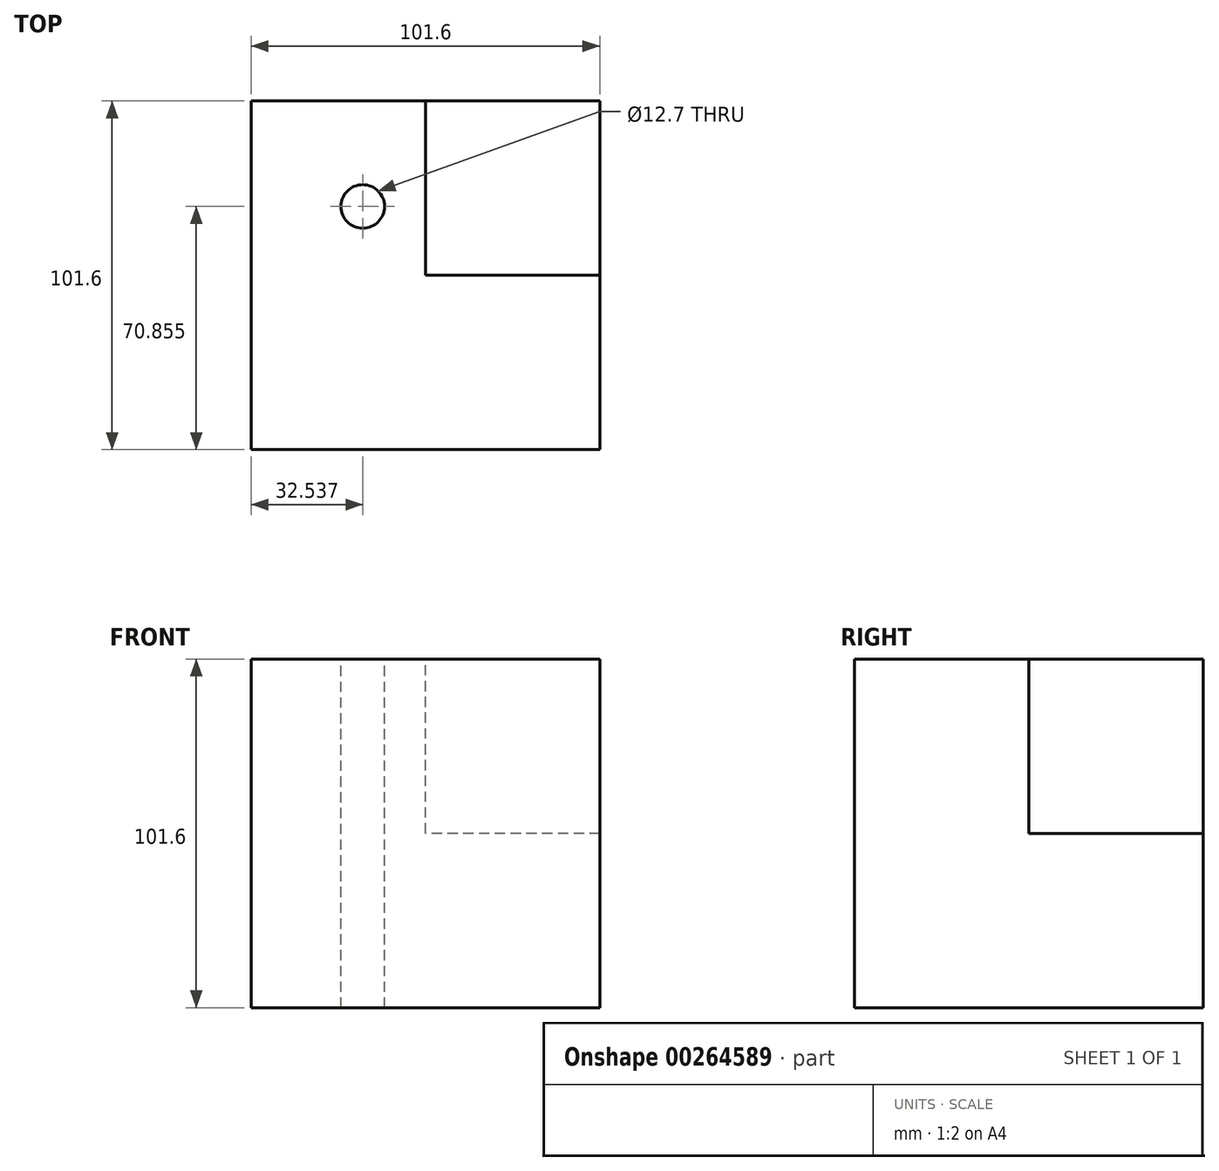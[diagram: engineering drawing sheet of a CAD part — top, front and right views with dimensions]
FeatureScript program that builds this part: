
annotation { "Feature Type Name" : "Feature", "Feature Type Description" : "" }
export const myFeature = defineFeature(function(context is Context, id is Id, definition is map)
    precondition{}
    {
        {
            var Q0;
            Q0=qCreatedBy(makeId("Front.planeOp"),FACE);
            var sketch = newSketch(context, id + "F0", { "sketchPlane" : qUnion([Q0])});
            skLineSegment(sketch, "E0.bottom", {"start": v(0, 0) * mm, "end": v(-101.6, 0) * mm});
            skLineSegment(sketch, "E0.top", {"start": v(0, 101.6) * mm, "end": v(-101.6, 101.6) * mm});
            skLineSegment(sketch, "E0.left", {"start": v(0, 0) * mm, "end": v(0, 101.6) * mm});
            skLineSegment(sketch, "E0.right", {"start": v(-101.6, 0) * mm, "end": v(-101.6, 101.6) * mm});
            skSolve(sketch);
        }
        {
            var Q0;
            Q0 = qSketchRegion(id + "F0", true);
            extrude(context, id + "F1", {"entities" : qUnion([Q0]), "depth" : 101.6 * mm});
        }
        {
            var Q0;
            Q0=makeQuery(id+"F1.opExtrude","SWEPT_FACE",FACE,{"disambiguationData":[OSD([sQuery(id+"F0.wireOp",EDGE,"E0.top")])]});
            var sketch = newSketch(context, id + "F2", { "sketchPlane" : qUnion([Q0])});
            skCircle(sketch, "E1", {"center": v(-69.06, -30.75) * mm, "radius": 6.35 * mm});
            skSolve(sketch);
        }
        {
            var Q0;
            Q0 = qSketchRegion(id + "F2", true);
            extrude(context, id + "F3", {"entities" : qUnion([Q0]), "operationType" : NewBodyOperationType.REMOVE, "oppositeDirection" : true, "depth" : 101.6 * mm});
        }
        {
            var Q0;
            Q0=makeQuery(id+"F1.opExtrude","SWEPT_FACE",FACE,{"disambiguationData":[OSD([sQuery(id+"F0.wireOp",EDGE,"E0.top")])]});
            var sketch = newSketch(context, id + "F4", { "sketchPlane" : qUnion([Q0])});
            skLineSegment(sketch, "E2.bottom", {"start": v(0, 0) * mm, "end": v(-50.8, 0) * mm});
            skLineSegment(sketch, "E2.top", {"start": v(0, -50.8) * mm, "end": v(-50.8, -50.8) * mm});
            skLineSegment(sketch, "E2.left", {"start": v(0, 0) * mm, "end": v(0, -50.8) * mm});
            skLineSegment(sketch, "E2.right", {"start": v(-50.8, 0) * mm, "end": v(-50.8, -50.8) * mm});
            skSolve(sketch);
        }
        {
            var Q0;
            Q0 = qSketchRegion(id + "F4", true);
            extrude(context, id + "F5", {"entities" : qUnion([Q0]), "operationType" : NewBodyOperationType.REMOVE, "oppositeDirection" : true, "depth" : 50.8 * mm});
        }
    });
